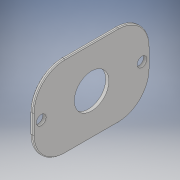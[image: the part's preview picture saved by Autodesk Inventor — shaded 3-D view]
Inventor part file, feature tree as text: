
AUTODESK INVENTOR PART (.ipt)
format: ipt  version: 2018 (Build 220112000, 112)  size: 151,552 bytes
history: native  units: mm
features: extrude x1, fillet x1, sketch x1
ambient origin geometry x8: Origin, YZ Plane, XZ Plane, XY Plane, X Axis, Y Axis, Z Axis, Center Point
bodies: Solid1 (feature_tree)
feature tree (3):
  extrude  "Extrusion1"  Depth=0.25mm
  fillet  "Fillet1"  Radius=37.0mm
  sketch  "Sketch1"  dims[d0=11.0mm d1=2.5mm d2=37.0mm d3=26.0mm d4=3.1mm d5=10.0mm d6=1.0mm d7=0.0mm d8=0.25mm]
